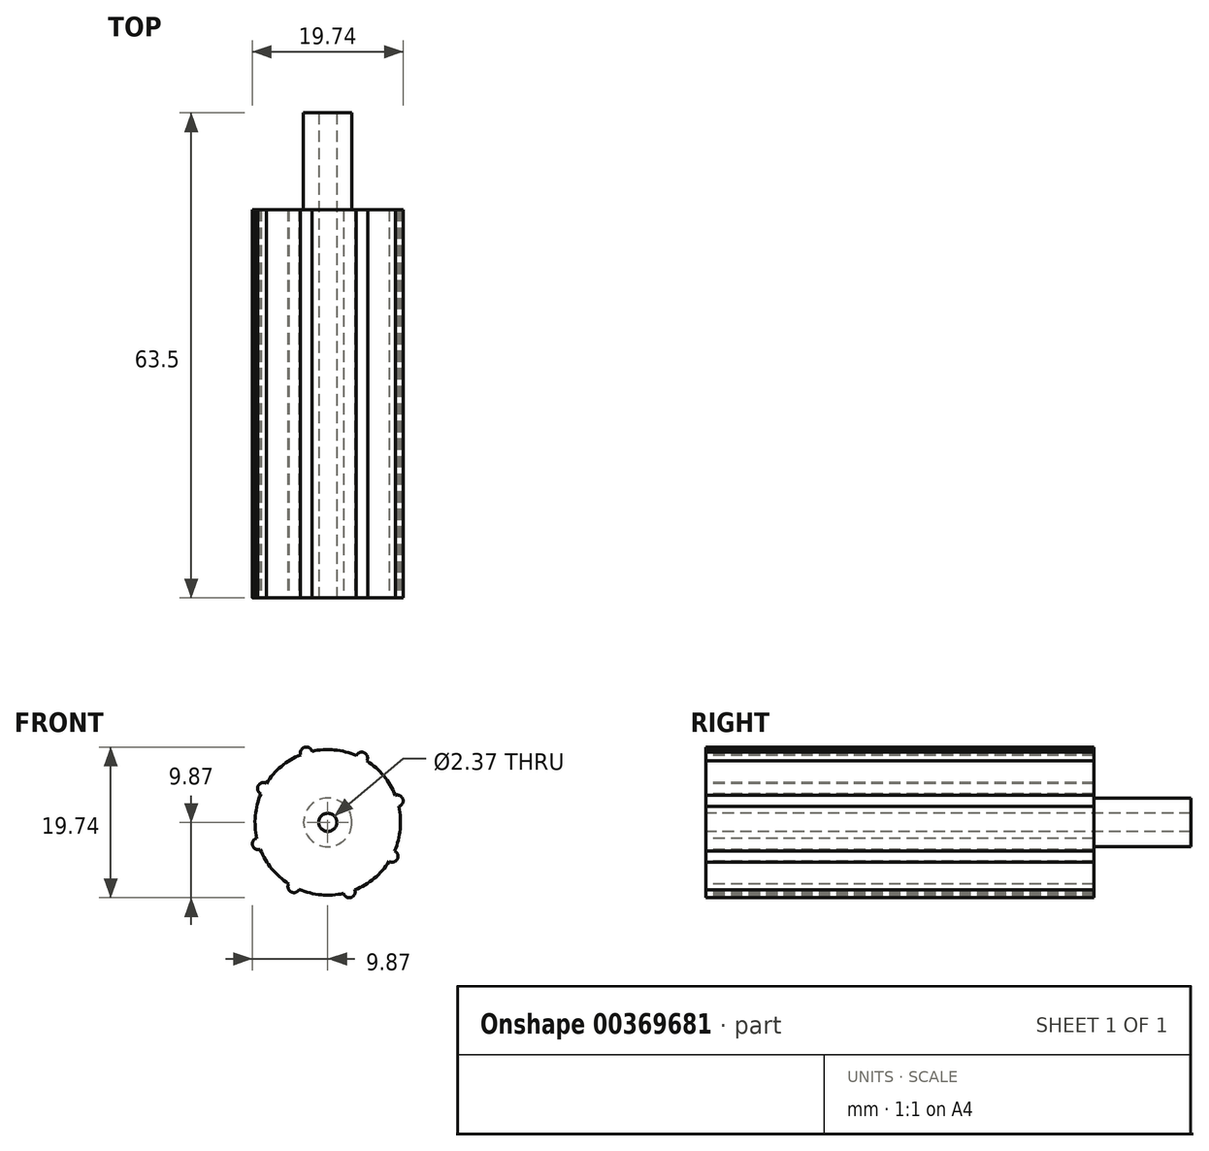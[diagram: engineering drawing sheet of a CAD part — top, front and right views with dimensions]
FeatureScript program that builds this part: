
annotation { "Feature Type Name" : "Feature", "Feature Type Description" : "" }
export const myFeature = defineFeature(function(context is Context, id is Id, definition is map)
    precondition{}
    {
        {
            assignVariable(context, id + "F0", {"name" : "DriveRollerLength", "anyValue" : 50.8 * mm});
        }
        {
            assignVariable(context, id + "F1", {"name" : "ShaftLength1", "anyValue" : 9.52 * mm});
        }
        {
            assignVariable(context, id + "F2", {"name" : "ShaftLength2", "anyValue" : 12.7 * mm});
        }
        {
            assignVariable(context, id + "F3", {"name" : "ShaftScrewHoleDepth", "anyValue" : 9.52 * mm});
        }
        {
            var Q0;
            Q0=qCreatedBy(makeId("Front.planeOp"),FACE);
            var sketch = newSketch(context, id + "F4", { "sketchPlane" : qUnion([Q0])});
            skCircle(sketch, "E0", {"center": v(0, 0) * mm, "radius": 9.53 * mm});
            skSolve(sketch);
        }
        {
            var Q0;
            Q0=qCreatedBy(makeId("Front.planeOp"),FACE);
            var sketch = newSketch(context, id + "F5", { "sketchPlane" : qUnion([Q0])});
            skCircle(sketch, "E1", {"center": v(-2.82, 9.1) * mm, "radius": 0.77 * mm});
            skCircle(sketch, "E2.1.0", {"center": v(4.44, 8.43) * mm, "radius": 0.77 * mm});
            skCircle(sketch, "E2.2.0", {"center": v(9.1, 2.82) * mm, "radius": 0.77 * mm});
            skCircle(sketch, "E2.3.0", {"center": v(8.43, -4.44) * mm, "radius": 0.77 * mm});
            skCircle(sketch, "E2.4.0", {"center": v(2.82, -9.1) * mm, "radius": 0.77 * mm});
            skPoint(sketch, "E2.center", {"position": v(0, 0) * mm});
            skLineSegment(sketch, "E2.anchor1", {"start": v(0, 0) * mm, "end": v(-2.82, 9.1) * mm, "construction": true});
            skLineSegment(sketch, "E2.anchor2", {"start": v(0, 0) * mm, "end": v(-8.43, 4.44) * mm, "construction": true});
            skCircle(sketch, "E3.1.5.0", {"center": v(-4.44, -8.43) * mm, "radius": 0.77 * mm});
            skCircle(sketch, "E3.1.6.0", {"center": v(-9.1, -2.82) * mm, "radius": 0.77 * mm});
            skCircle(sketch, "E3.1.7.0", {"center": v(-8.43, 4.44) * mm, "radius": 0.77 * mm});
            skSolve(sketch);
        }
        {
            var Q0;
            Q0 = qSketchRegion(id + "F4", true);
            extrude(context, id + "F6", {"entities" : qUnion([Q0]), "oppositeDirection" : true, "depth" : getVariable(context, 'DriveRollerLength')});
        }
        {
            var Q0;
            Q0 = qSketchRegion(id + "F5", true);
            extrude(context, id + "F7", {"entities" : qUnion([Q0]), "operationType" : NewBodyOperationType.ADD, "oppositeDirection" : true, "depth" : getVariable(context, 'DriveRollerLength')});
        }
        {
            var Q0;
            Q0=qCreatedBy(makeId("Front.planeOp"),FACE);
            var sketch = newSketch(context, id + "F8", { "sketchPlane" : qUnion([Q0])});
            skCircle(sketch, "E4", {"center": v(0, 0) * mm, "radius": 0.51 * mm});
            skSolve(sketch);
        }
        {
            var Q0;
            Q0=qCreatedBy(makeId("Front.planeOp"),FACE);
            var sketch = newSketch(context, id + "F9", { "sketchPlane" : qUnion([Q0])});
            skCircle(sketch, "E5", {"center": v(0, 0) * mm, "radius": 3.18 * mm});
            skSolve(sketch);
        }
        {
            var Q0;
            Q0 = qSketchRegion(id + "F8", true);
            extrude(context, id + "F10", {"entities" : qUnion([Q0]), "operationType" : NewBodyOperationType.REMOVE, "oppositeDirection" : true, "depth" : getVariable(context, 'ShaftLength1')});
        }
        {
            var Q0;
            Q0 = qSketchRegion(id + "F9", true);
            extrude(context, id + "F11", {"entities" : qUnion([Q0]), "operationType" : NewBodyOperationType.ADD, "oppositeDirection" : true, "depth" : getVariable(context, 'DriveRollerLength') + getVariable(context, 'ShaftLength2')});
        }
        {
            var Q0;
            Q0=qCreatedBy(makeId("Front.planeOp"),FACE);
            var sketch = newSketch(context, id + "F12", { "sketchPlane" : qUnion([Q0])});
            skCircle(sketch, "E6", {"center": v(0, 0) * mm, "radius": 1.19 * mm});
            skSolve(sketch);
        }
        {
            var Q0;
            Q0 = qSketchRegion(id + "F12", true);
            extrude(context, id + "F13", {"entities" : qUnion([Q0]), "operationType" : NewBodyOperationType.REMOVE, "oppositeDirection" : true, "depth" : getVariable(context, 'DriveRollerLength') + getVariable(context, 'ShaftLength1') + getVariable(context, 'ShaftScrewHoleDepth')});
        }
    });
